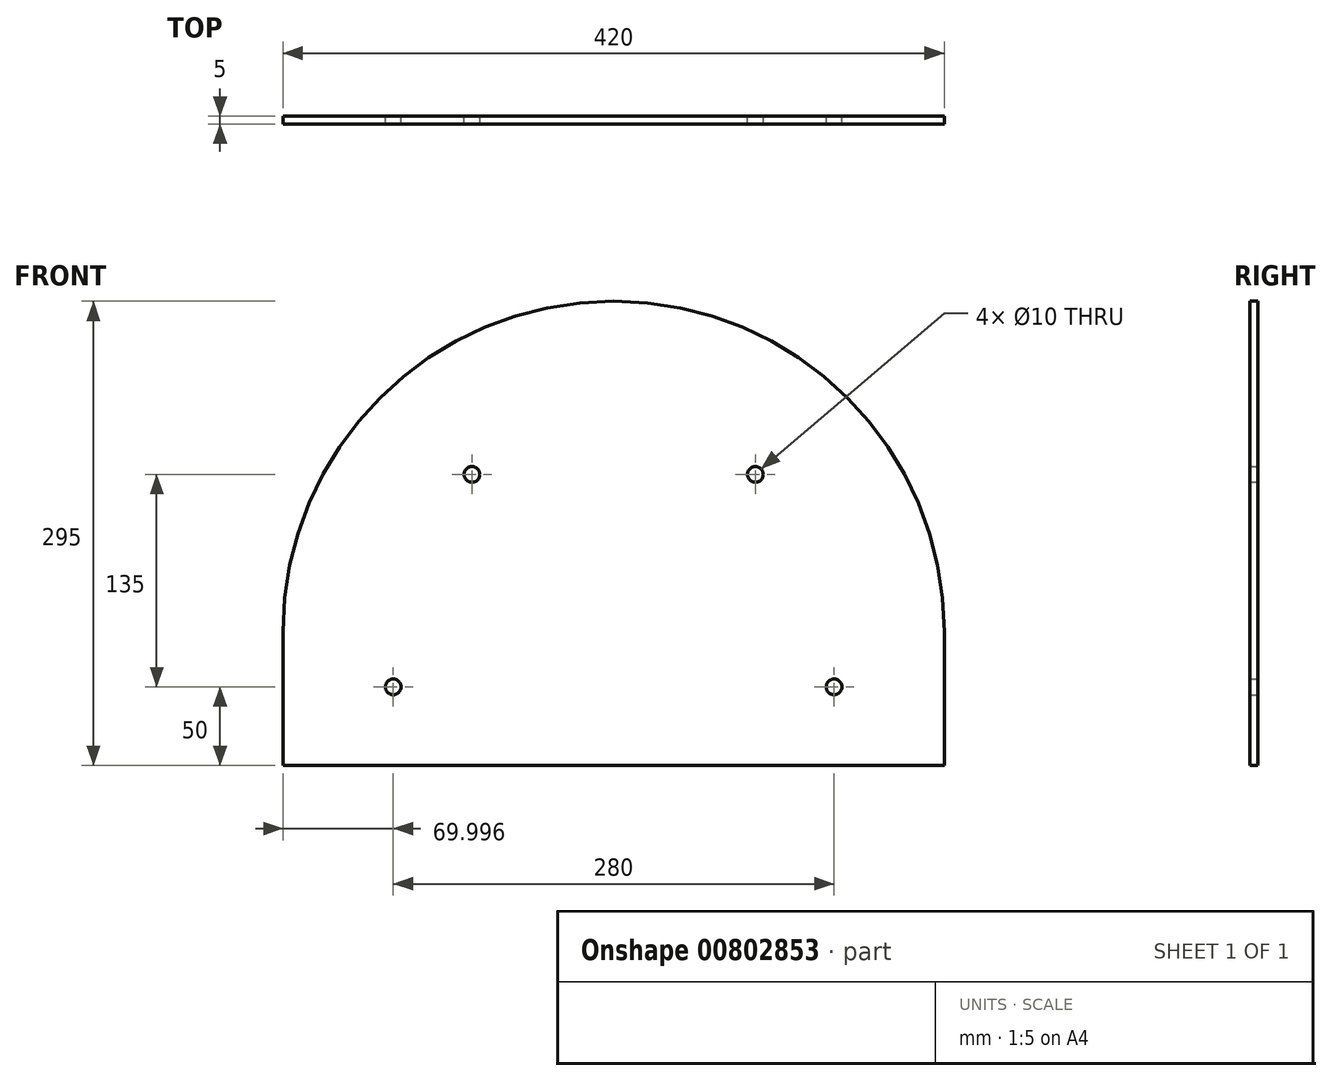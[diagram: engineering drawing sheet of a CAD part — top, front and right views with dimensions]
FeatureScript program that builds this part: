
annotation { "Feature Type Name" : "Feature", "Feature Type Description" : "" }
export const myFeature = defineFeature(function(context is Context, id is Id, definition is map)
    precondition{}
    {
        {
            var Q0;
            Q0=qCreatedBy(makeId("Front.planeOp"),FACE);
            var sketch = newSketch(context, id + "F0", { "sketchPlane" : qUnion([Q0])});
            skArc(sketch, "E0", {"start": v(-29.06, 35) * mm, "mid": v(-239.06, 245) * mm, "end": v(-449.06, 35) * mm});
            skLineSegment(sketch, "E1", {"start": v(-449.06, 35) * mm, "end": v(-449.06, -50) * mm});
            skLineSegment(sketch, "E2", {"start": v(-449.06, -50) * mm, "end": v(-29.06, -50) * mm});
            skLineSegment(sketch, "E3", {"start": v(-29.06, 35) * mm, "end": v(-29.06, -50) * mm});
            skCircle(sketch, "E4", {"center": v(-149.06, 135) * mm, "radius": 5 * mm});
            skCircle(sketch, "E5", {"center": v(-329.06, 135) * mm, "radius": 5 * mm});
            skCircle(sketch, "E6", {"center": v(-99.06, 0) * mm, "radius": 5 * mm});
            skCircle(sketch, "E7", {"center": v(-379.06, 0) * mm, "radius": 5 * mm});
            skSolve(sketch);
        }
        {
            var Q0;
            Q0=makeQuery(id+"F0.imprint","IMPRINT",FACE,{"disambiguationData":[TD([[makeQuery(id+"F0.imprint","IMPRINT",EDGE,{"derivedFrom":sQuery(id+"F0.wireOp",EDGE,"E0")}),1.0]])]});
            extrude(context, id + "F1", {"entities" : qUnion([Q0]), "depth" : 5 * mm, "offsetDistance" : 25.4 * mm});
        }
    });
